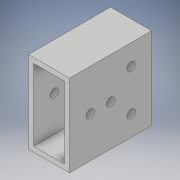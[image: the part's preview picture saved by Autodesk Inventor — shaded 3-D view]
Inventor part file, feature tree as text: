
AUTODESK INVENTOR PART (.ipt)
format: ipt  version: 2018 (Build 220112000, 112)  size: 127,488 bytes
history: native  units: in
note: dims shown in document units (in); Inventor stores cm internally (conversion verified against a paired STEP export)
features: extrude x3, sketch x3
ambient origin geometry x8: Origin, YZ Plane, XZ Plane, XY Plane, X Axis, Y Axis, Z Axis, Center Point
bodies: Solid1 (feature_tree)
feature tree (6):
  extrude  "Extrusion1"  Depth=2.0in
  extrude  "Extrusion2"  Depth=2.0in TaperAngle=0.0deg
  extrude  "Extrusion3"  Depth=1.0in
  sketch  "Sketch1"  dims[d0=1.0in d1=2.0in]
  sketch  "Sketch2"  dims[d2=0.125in d3=2.0in d4=0.0in]
  sketch  "Sketch3"  dims[d5=0.5in d6=0.5in d7=1.0in d8=0.2031in d9=2.0in d10=0.0in d11=0.5in d12=0.5in d13=0.2031in d14=1.0in d15=0.0in]
